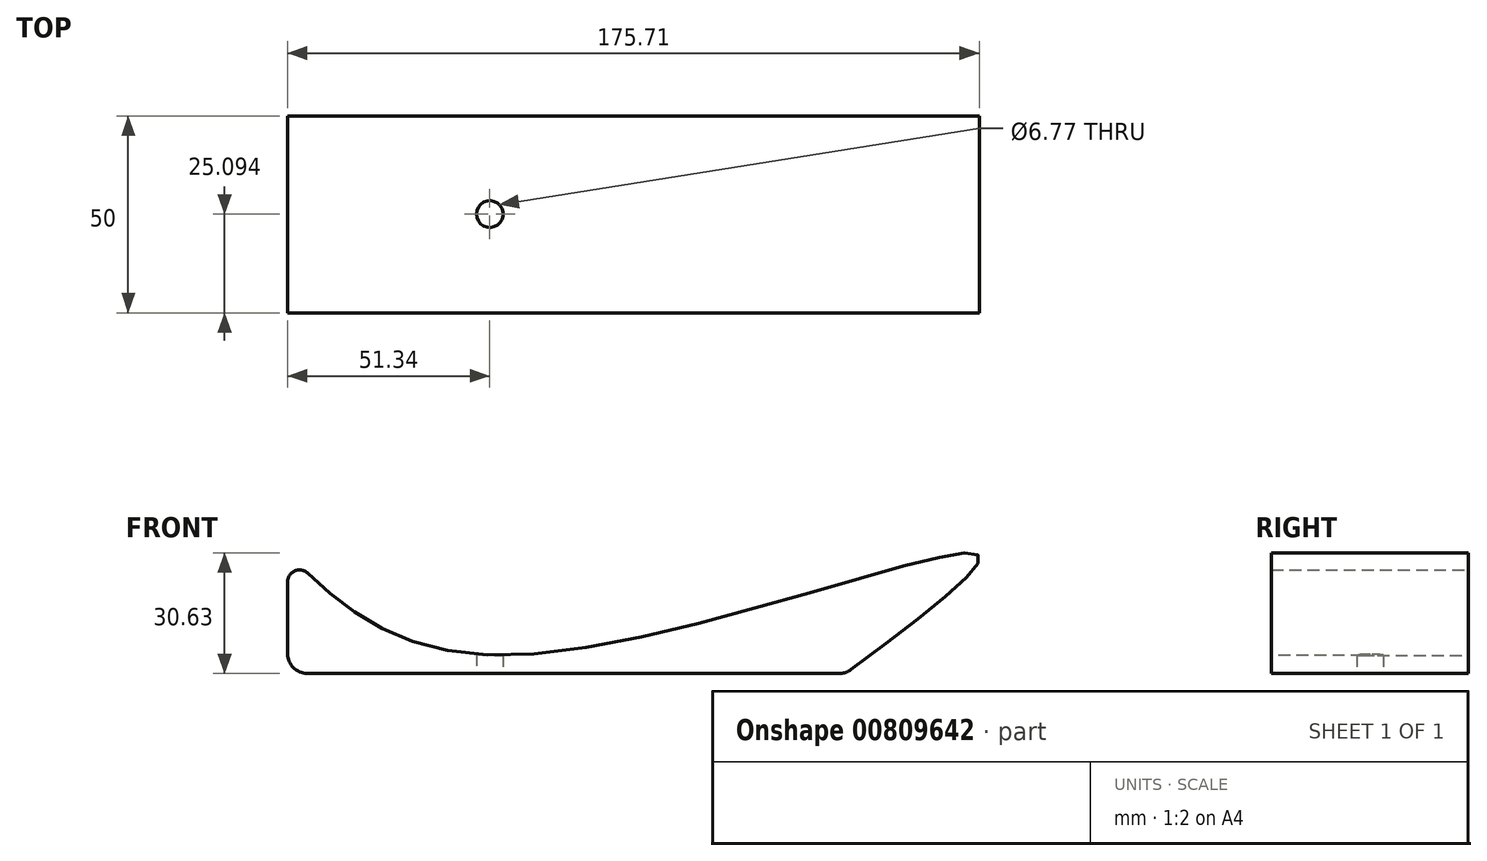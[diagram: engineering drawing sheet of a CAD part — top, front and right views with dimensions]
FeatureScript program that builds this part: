
annotation { "Feature Type Name" : "Feature", "Feature Type Description" : "" }
export const myFeature = defineFeature(function(context is Context, id is Id, definition is map)
    precondition{}
    {
        {
            var Q0;
            Q0=qCreatedBy(makeId("Front.planeOp"),FACE);
            var sketch = newSketch(context, id + "F0", { "sketchPlane" : qUnion([Q0])});
            skLineSegment(sketch, "E0.bottom", {"start": v(0, 0) * mm, "end": v(180, 0) * mm});
            skLineSegment(sketch, "E0.top", {"start": v(0, 30) * mm, "end": v(180, 30) * mm});
            skLineSegment(sketch, "E0.left", {"start": v(0, 0) * mm, "end": v(0, 30) * mm});
            skLineSegment(sketch, "E0.right", {"start": v(180, 0) * mm, "end": v(180, 30) * mm});
            skSolve(sketch);
        }
        {
            var Q0;
            Q0 = qSketchRegion(id + "F0", true);
            extrude(context, id + "F1", {"entities" : qUnion([Q0]), "depth" : 50 * mm, "offsetDistance" : 25 * mm});
        }
        {
            var Q0;
            Q0=qCreatedBy(makeId("Front.planeOp"),FACE);
            var sketch = newSketch(context, id + "F2", { "sketchPlane" : qUnion([Q0])});
            skLineSegment(sketch, "E1", {"start": v(6.92, 0) * mm, "end": v(142.07, 0) * mm});
            skFitSpline(sketch, "E2", {"points": [v(1.92, 30.3) * mm, v(58.33, 4.66) * mm, v(176.95, 30.3) * mm, v(143.73, 0) * mm], "startDerivative": vector(133.63, -128.6) * mm, "endDerivative": vector(-216.12, -160.78) * mm});
            skLineSegment(sketch, "E3", {"start": v(1.92, 23.3) * mm, "end": v(1.92, 5) * mm});
            skPoint(sketch, "E4.visualSharp", {"position": v(1.92, 0) * mm});
            skArc(sketch, "E4.filletArc", {"start": v(1.92, 5) * mm, "mid": v(3.38, 1.46) * mm, "end": v(6.92, 0) * mm});
            skArc(sketch, "E5.filletArc", {"start": v(142.07, 0) * mm, "mid": v(143.65, 0.25) * mm, "end": v(145.06, 0.99) * mm});
            skArc(sketch, "E6.filletArc", {"start": v(6.96, 25.5) * mm, "mid": v(3.72, 26.05) * mm, "end": v(1.92, 23.3) * mm});
            skSolve(sketch);
        }
        {
            var Q0;
            Q0 = qSketchRegion(id + "F2", true);
            var Q1;
            Q1=sQuery(id+"F2.wireOp",EDGE,"E2");
            var Q2;
            Q2=makeQuery(id+"F1.opExtrude","CAP_FACE",FACE,{"disambiguationData":[OSD([sQuery(id+"F0.wireOp",EDGE,"E0.bottom"),sQuery(id+"F0.wireOp",EDGE,"E0.top"),sQuery(id+"F0.wireOp",EDGE,"E0.left"),sQuery(id+"F0.wireOp",EDGE,"E0.right")])],"isStart":false});
            extrude(context, id + "F3", {"entities" : qUnion([Q0]), "surfaceEntities" : qUnion([Q1]), "endBound" : BoundingType.UP_TO_SURFACE, "depth" : 25 * mm, "endBoundEntityFace" : qUnion([Q2]), "offsetDistance" : 25 * mm});
        }
        {
            var Q0;
            Q0=makeQuery(id+"F1.opExtrude","SWEPT_BODY",BODY,{"disambiguationData":[OSD([sQuery(id+"F0.wireOp",EDGE,"E0.bottom"),sQuery(id+"F0.wireOp",EDGE,"E0.top"),sQuery(id+"F0.wireOp",EDGE,"E0.left"),sQuery(id+"F0.wireOp",EDGE,"E0.right")])]});
            deleteBodies(context, id + "F4", {"entities" : qUnion([Q0])});
        }
        {
            var Q0;
            Q0=makeQuery(id+"F3.opExtrude","SWEPT_FACE",FACE,{"disambiguationData":[OSD([sQuery(id+"F2.wireOp",EDGE,"E1")])]});
            var sketch = newSketch(context, id + "F5", { "sketchPlane" : qUnion([Q0])});
            skCircle(sketch, "E7", {"center": v(53.26, 24.9) * mm, "radius": 3.38 * mm});
            skSolve(sketch);
        }
        {
            var Q0;
            Q0 = qSketchRegion(id + "F5", true);
            extrude(context, id + "F6", {"entities" : qUnion([Q0]), "operationType" : NewBodyOperationType.REMOVE, "oppositeDirection" : true, "depth" : 25 * mm, "offsetDistance" : 25 * mm});
        }
    });
